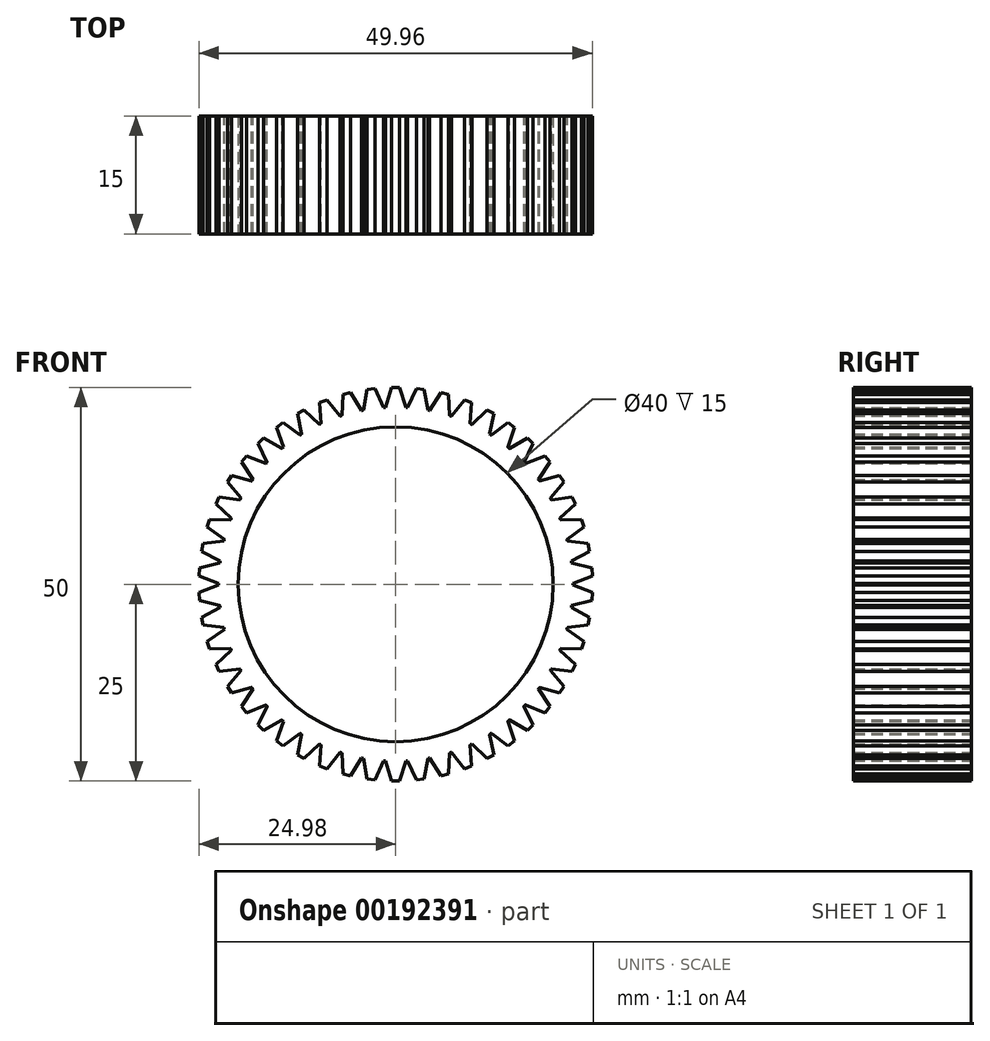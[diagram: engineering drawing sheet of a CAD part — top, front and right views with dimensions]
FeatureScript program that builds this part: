
annotation { "Feature Type Name" : "Feature", "Feature Type Description" : "" }
export const myFeature = defineFeature(function(context is Context, id is Id, definition is map)
    precondition{}
    {
        {
            var Q0;
            Q0=qCreatedBy(makeId("Front.planeOp"),FACE);
            var sketch = newSketch(context, id + "F0", { "sketchPlane" : qUnion([Q0])});
            skCircle(sketch, "E0", {"center": v(0, 0) * mm, "radius": 22.5 * mm});
            skLineSegment(sketch, "E1", {"start": v(-0.5, 25) * mm, "end": v(-1.3, 22.46) * mm});
            skLineSegment(sketch, "E2.MirrorCS", {"start": v(0.5, 25) * mm, "end": v(1.3, 22.46) * mm});
            skLineSegment(sketch, "E3", {"start": v(-0.5, 25) * mm, "end": v(0.5, 25) * mm});
            skLineSegment(sketch, "E4.1.0", {"start": v(-3.63, 24.74) * mm, "end": v(-2.64, 24.87) * mm});
            skLineSegment(sketch, "E4.1.1", {"start": v(-3.63, 24.74) * mm, "end": v(-4.1, 22.12) * mm});
            skLineSegment(sketch, "E4.1.2", {"start": v(-2.64, 24.87) * mm, "end": v(-1.53, 22.45) * mm});
            skLineSegment(sketch, "E4.2.0", {"start": v(-6.7, 24.1) * mm, "end": v(-5.73, 24.34) * mm});
            skLineSegment(sketch, "E4.2.1", {"start": v(-6.7, 24.1) * mm, "end": v(-6.84, 21.44) * mm});
            skLineSegment(sketch, "E4.2.2", {"start": v(-5.73, 24.34) * mm, "end": v(-4.33, 22.08) * mm});
            skLineSegment(sketch, "E4.3.0", {"start": v(-9.67, 23.06) * mm, "end": v(-8.74, 23.43) * mm});
            skLineSegment(sketch, "E4.3.1", {"start": v(-9.67, 23.06) * mm, "end": v(-9.47, 20.4) * mm});
            skLineSegment(sketch, "E4.3.2", {"start": v(-8.74, 23.43) * mm, "end": v(-7.07, 21.36) * mm});
            skLineSegment(sketch, "E4.4.0", {"start": v(-12.48, 21.67) * mm, "end": v(-11.6, 22.15) * mm});
            skLineSegment(sketch, "E4.4.1", {"start": v(-12.48, 21.67) * mm, "end": v(-11.95, 19.06) * mm});
            skLineSegment(sketch, "E4.4.2", {"start": v(-11.6, 22.15) * mm, "end": v(-9.69, 20.3) * mm});
            skLineSegment(sketch, "E4.5.0", {"start": v(-15.1, 19.93) * mm, "end": v(-14.3, 20.52) * mm});
            skLineSegment(sketch, "E4.5.1", {"start": v(-15.1, 19.93) * mm, "end": v(-14.25, 17.41) * mm});
            skLineSegment(sketch, "E4.5.2", {"start": v(-14.3, 20.52) * mm, "end": v(-12.16, 18.93) * mm});
            skLineSegment(sketch, "E4.6.0", {"start": v(-17.48, 17.88) * mm, "end": v(-16.75, 18.57) * mm});
            skLineSegment(sketch, "E4.6.1", {"start": v(-17.48, 17.88) * mm, "end": v(-16.32, 15.49) * mm});
            skLineSegment(sketch, "E4.6.2", {"start": v(-16.75, 18.57) * mm, "end": v(-14.43, 17.26) * mm});
            skLineSegment(sketch, "E4.7.0", {"start": v(-19.58, 15.55) * mm, "end": v(-18.94, 16.32) * mm});
            skLineSegment(sketch, "E4.7.1", {"start": v(-19.58, 15.55) * mm, "end": v(-18.13, 13.32) * mm});
            skLineSegment(sketch, "E4.7.2", {"start": v(-18.94, 16.32) * mm, "end": v(-16.48, 15.31) * mm});
            skLineSegment(sketch, "E4.8.0", {"start": v(-21.38, 12.97) * mm, "end": v(-20.84, 13.82) * mm});
            skLineSegment(sketch, "E4.8.1", {"start": v(-21.38, 12.97) * mm, "end": v(-19.66, 10.94) * mm});
            skLineSegment(sketch, "E4.8.2", {"start": v(-20.84, 13.82) * mm, "end": v(-18.27, 13.13) * mm});
            skLineSegment(sketch, "E4.9.0", {"start": v(-22.83, 10.2) * mm, "end": v(-22.4, 11.1) * mm});
            skLineSegment(sketch, "E4.9.1", {"start": v(-22.83, 10.2) * mm, "end": v(-20.88, 8.4) * mm});
            skLineSegment(sketch, "E4.9.2", {"start": v(-22.4, 11.1) * mm, "end": v(-19.77, 10.73) * mm});
            skLineSegment(sketch, "E4.10.0", {"start": v(-23.93, 7.25) * mm, "end": v(-23.62, 8.2) * mm});
            skLineSegment(sketch, "E4.10.1", {"start": v(-23.93, 7.25) * mm, "end": v(-21.76, 5.71) * mm});
            skLineSegment(sketch, "E4.10.2", {"start": v(-23.62, 8.2) * mm, "end": v(-20.96, 8.17) * mm});
            skLineSegment(sketch, "E4.11.0", {"start": v(-24.65, 4.2) * mm, "end": v(-24.46, 5.18) * mm});
            skLineSegment(sketch, "E4.11.1", {"start": v(-24.65, 4.2) * mm, "end": v(-22.3, 2.94) * mm});
            skLineSegment(sketch, "E4.11.2", {"start": v(-24.46, 5.18) * mm, "end": v(-21.82, 5.48) * mm});
            skLineSegment(sketch, "E4.12.0", {"start": v(-24.98, 1.07) * mm, "end": v(-24.92, 2.07) * mm});
            skLineSegment(sketch, "E4.12.1", {"start": v(-24.98, 1.07) * mm, "end": v(-22.5, 0.12) * mm});
            skLineSegment(sketch, "E4.12.2", {"start": v(-24.92, 2.07) * mm, "end": v(-22.34, 2.7) * mm});
            skLineSegment(sketch, "E4.13.0", {"start": v(-24.92, -2.07) * mm, "end": v(-24.98, -1.07) * mm});
            skLineSegment(sketch, "E4.13.1", {"start": v(-24.92, -2.07) * mm, "end": v(-22.34, -2.7) * mm});
            skLineSegment(sketch, "E4.13.2", {"start": v(-24.98, -1.07) * mm, "end": v(-22.5, -0.12) * mm});
            skLineSegment(sketch, "E4.14.0", {"start": v(-24.46, -5.18) * mm, "end": v(-24.65, -4.2) * mm});
            skLineSegment(sketch, "E4.14.1", {"start": v(-24.46, -5.18) * mm, "end": v(-21.82, -5.48) * mm});
            skLineSegment(sketch, "E4.14.2", {"start": v(-24.65, -4.2) * mm, "end": v(-22.3, -2.94) * mm});
            skLineSegment(sketch, "E4.15.0", {"start": v(-23.62, -8.2) * mm, "end": v(-23.93, -7.25) * mm});
            skLineSegment(sketch, "E4.15.1", {"start": v(-23.62, -8.2) * mm, "end": v(-20.96, -8.17) * mm});
            skLineSegment(sketch, "E4.15.2", {"start": v(-23.93, -7.25) * mm, "end": v(-21.76, -5.71) * mm});
            skLineSegment(sketch, "E4.16.0", {"start": v(-22.4, -11.1) * mm, "end": v(-22.83, -10.2) * mm});
            skLineSegment(sketch, "E4.16.1", {"start": v(-22.4, -11.1) * mm, "end": v(-19.77, -10.73) * mm});
            skLineSegment(sketch, "E4.16.2", {"start": v(-22.83, -10.2) * mm, "end": v(-20.88, -8.4) * mm});
            skLineSegment(sketch, "E4.17.0", {"start": v(-20.84, -13.82) * mm, "end": v(-21.38, -12.97) * mm});
            skLineSegment(sketch, "E4.17.1", {"start": v(-20.84, -13.82) * mm, "end": v(-18.27, -13.13) * mm});
            skLineSegment(sketch, "E4.17.2", {"start": v(-21.38, -12.97) * mm, "end": v(-19.66, -10.94) * mm});
            skLineSegment(sketch, "E4.18.0", {"start": v(-18.94, -16.32) * mm, "end": v(-19.58, -15.55) * mm});
            skLineSegment(sketch, "E4.18.1", {"start": v(-18.94, -16.32) * mm, "end": v(-16.48, -15.31) * mm});
            skLineSegment(sketch, "E4.18.2", {"start": v(-19.58, -15.55) * mm, "end": v(-18.13, -13.32) * mm});
            skLineSegment(sketch, "E4.19.0", {"start": v(-16.75, -18.57) * mm, "end": v(-17.48, -17.88) * mm});
            skLineSegment(sketch, "E4.19.1", {"start": v(-16.75, -18.57) * mm, "end": v(-14.43, -17.26) * mm});
            skLineSegment(sketch, "E4.19.2", {"start": v(-17.48, -17.88) * mm, "end": v(-16.32, -15.49) * mm});
            skLineSegment(sketch, "E4.20.0", {"start": v(-14.3, -20.52) * mm, "end": v(-15.1, -19.93) * mm});
            skLineSegment(sketch, "E4.20.1", {"start": v(-14.3, -20.52) * mm, "end": v(-12.16, -18.93) * mm});
            skLineSegment(sketch, "E4.20.2", {"start": v(-15.1, -19.93) * mm, "end": v(-14.25, -17.41) * mm});
            skLineSegment(sketch, "E4.21.0", {"start": v(-11.6, -22.15) * mm, "end": v(-12.48, -21.67) * mm});
            skLineSegment(sketch, "E4.21.1", {"start": v(-11.6, -22.15) * mm, "end": v(-9.69, -20.3) * mm});
            skLineSegment(sketch, "E4.21.2", {"start": v(-12.48, -21.67) * mm, "end": v(-11.95, -19.06) * mm});
            skLineSegment(sketch, "E4.22.0", {"start": v(-8.74, -23.43) * mm, "end": v(-9.67, -23.06) * mm});
            skLineSegment(sketch, "E4.22.1", {"start": v(-8.74, -23.43) * mm, "end": v(-7.07, -21.36) * mm});
            skLineSegment(sketch, "E4.22.2", {"start": v(-9.67, -23.06) * mm, "end": v(-9.47, -20.4) * mm});
            skLineSegment(sketch, "E4.23.0", {"start": v(-5.73, -24.34) * mm, "end": v(-6.7, -24.1) * mm});
            skLineSegment(sketch, "E4.23.1", {"start": v(-5.73, -24.34) * mm, "end": v(-4.33, -22.08) * mm});
            skLineSegment(sketch, "E4.23.2", {"start": v(-6.7, -24.1) * mm, "end": v(-6.84, -21.44) * mm});
            skLineSegment(sketch, "E4.24.0", {"start": v(-2.64, -24.87) * mm, "end": v(-3.63, -24.74) * mm});
            skLineSegment(sketch, "E4.24.1", {"start": v(-2.64, -24.87) * mm, "end": v(-1.53, -22.45) * mm});
            skLineSegment(sketch, "E4.24.2", {"start": v(-3.63, -24.74) * mm, "end": v(-4.1, -22.12) * mm});
            skLineSegment(sketch, "E4.25.0", {"start": v(0.5, -25) * mm, "end": v(-0.5, -25) * mm});
            skLineSegment(sketch, "E4.25.1", {"start": v(0.5, -25) * mm, "end": v(1.3, -22.46) * mm});
            skLineSegment(sketch, "E4.25.2", {"start": v(-0.5, -25) * mm, "end": v(-1.3, -22.46) * mm});
            skLineSegment(sketch, "E4.26.0", {"start": v(3.63, -24.74) * mm, "end": v(2.64, -24.87) * mm});
            skLineSegment(sketch, "E4.26.1", {"start": v(3.63, -24.74) * mm, "end": v(4.1, -22.12) * mm});
            skLineSegment(sketch, "E4.26.2", {"start": v(2.64, -24.87) * mm, "end": v(1.53, -22.45) * mm});
            skLineSegment(sketch, "E4.27.0", {"start": v(6.7, -24.1) * mm, "end": v(5.73, -24.34) * mm});
            skLineSegment(sketch, "E4.27.1", {"start": v(6.7, -24.1) * mm, "end": v(6.84, -21.44) * mm});
            skLineSegment(sketch, "E4.27.2", {"start": v(5.73, -24.34) * mm, "end": v(4.33, -22.08) * mm});
            skLineSegment(sketch, "E4.28.0", {"start": v(9.67, -23.06) * mm, "end": v(8.74, -23.43) * mm});
            skLineSegment(sketch, "E4.28.1", {"start": v(9.67, -23.06) * mm, "end": v(9.47, -20.4) * mm});
            skLineSegment(sketch, "E4.28.2", {"start": v(8.74, -23.43) * mm, "end": v(7.07, -21.36) * mm});
            skLineSegment(sketch, "E4.29.0", {"start": v(12.48, -21.67) * mm, "end": v(11.6, -22.15) * mm});
            skLineSegment(sketch, "E4.29.1", {"start": v(12.48, -21.67) * mm, "end": v(11.95, -19.06) * mm});
            skLineSegment(sketch, "E4.29.2", {"start": v(11.6, -22.15) * mm, "end": v(9.69, -20.3) * mm});
            skLineSegment(sketch, "E4.30.0", {"start": v(15.1, -19.93) * mm, "end": v(14.3, -20.52) * mm});
            skLineSegment(sketch, "E4.30.1", {"start": v(15.1, -19.93) * mm, "end": v(14.25, -17.41) * mm});
            skLineSegment(sketch, "E4.30.2", {"start": v(14.3, -20.52) * mm, "end": v(12.16, -18.93) * mm});
            skLineSegment(sketch, "E4.31.0", {"start": v(17.48, -17.88) * mm, "end": v(16.75, -18.57) * mm});
            skLineSegment(sketch, "E4.31.1", {"start": v(17.48, -17.88) * mm, "end": v(16.32, -15.49) * mm});
            skLineSegment(sketch, "E4.31.2", {"start": v(16.75, -18.57) * mm, "end": v(14.43, -17.26) * mm});
            skLineSegment(sketch, "E4.32.0", {"start": v(19.58, -15.55) * mm, "end": v(18.94, -16.32) * mm});
            skLineSegment(sketch, "E4.32.1", {"start": v(19.58, -15.55) * mm, "end": v(18.13, -13.32) * mm});
            skLineSegment(sketch, "E4.32.2", {"start": v(18.94, -16.32) * mm, "end": v(16.48, -15.31) * mm});
            skLineSegment(sketch, "E4.33.0", {"start": v(21.38, -12.97) * mm, "end": v(20.84, -13.82) * mm});
            skLineSegment(sketch, "E4.33.1", {"start": v(21.38, -12.97) * mm, "end": v(19.66, -10.94) * mm});
            skLineSegment(sketch, "E4.33.2", {"start": v(20.84, -13.82) * mm, "end": v(18.27, -13.13) * mm});
            skLineSegment(sketch, "E4.34.0", {"start": v(22.83, -10.2) * mm, "end": v(22.4, -11.1) * mm});
            skLineSegment(sketch, "E4.34.1", {"start": v(22.83, -10.2) * mm, "end": v(20.88, -8.4) * mm});
            skLineSegment(sketch, "E4.34.2", {"start": v(22.4, -11.1) * mm, "end": v(19.77, -10.73) * mm});
            skLineSegment(sketch, "E4.35.0", {"start": v(23.93, -7.25) * mm, "end": v(23.62, -8.2) * mm});
            skLineSegment(sketch, "E4.35.1", {"start": v(23.93, -7.25) * mm, "end": v(21.76, -5.71) * mm});
            skLineSegment(sketch, "E4.35.2", {"start": v(23.62, -8.2) * mm, "end": v(20.96, -8.17) * mm});
            skLineSegment(sketch, "E4.36.0", {"start": v(24.65, -4.2) * mm, "end": v(24.46, -5.18) * mm});
            skLineSegment(sketch, "E4.36.1", {"start": v(24.65, -4.2) * mm, "end": v(22.3, -2.94) * mm});
            skLineSegment(sketch, "E4.36.2", {"start": v(24.46, -5.18) * mm, "end": v(21.82, -5.48) * mm});
            skLineSegment(sketch, "E4.37.0", {"start": v(24.98, -1.07) * mm, "end": v(24.92, -2.07) * mm});
            skLineSegment(sketch, "E4.37.1", {"start": v(24.98, -1.07) * mm, "end": v(22.5, -0.12) * mm});
            skLineSegment(sketch, "E4.37.2", {"start": v(24.92, -2.07) * mm, "end": v(22.34, -2.7) * mm});
            skLineSegment(sketch, "E4.38.0", {"start": v(24.92, 2.07) * mm, "end": v(24.98, 1.07) * mm});
            skLineSegment(sketch, "E4.38.1", {"start": v(24.92, 2.07) * mm, "end": v(22.34, 2.7) * mm});
            skLineSegment(sketch, "E4.38.2", {"start": v(24.98, 1.07) * mm, "end": v(22.5, 0.12) * mm});
            skLineSegment(sketch, "E4.39.0", {"start": v(24.46, 5.18) * mm, "end": v(24.65, 4.2) * mm});
            skLineSegment(sketch, "E4.39.1", {"start": v(24.46, 5.18) * mm, "end": v(21.82, 5.48) * mm});
            skLineSegment(sketch, "E4.39.2", {"start": v(24.65, 4.2) * mm, "end": v(22.3, 2.94) * mm});
            skLineSegment(sketch, "E4.40.0", {"start": v(23.62, 8.2) * mm, "end": v(23.93, 7.25) * mm});
            skLineSegment(sketch, "E4.40.1", {"start": v(23.62, 8.2) * mm, "end": v(20.96, 8.17) * mm});
            skLineSegment(sketch, "E4.40.2", {"start": v(23.93, 7.25) * mm, "end": v(21.76, 5.71) * mm});
            skLineSegment(sketch, "E4.41.0", {"start": v(22.4, 11.1) * mm, "end": v(22.83, 10.2) * mm});
            skLineSegment(sketch, "E4.41.1", {"start": v(22.4, 11.1) * mm, "end": v(19.77, 10.73) * mm});
            skLineSegment(sketch, "E4.41.2", {"start": v(22.83, 10.2) * mm, "end": v(20.88, 8.4) * mm});
            skLineSegment(sketch, "E4.42.0", {"start": v(20.84, 13.82) * mm, "end": v(21.38, 12.97) * mm});
            skLineSegment(sketch, "E4.42.1", {"start": v(20.84, 13.82) * mm, "end": v(18.27, 13.13) * mm});
            skLineSegment(sketch, "E4.42.2", {"start": v(21.38, 12.97) * mm, "end": v(19.66, 10.94) * mm});
            skLineSegment(sketch, "E4.43.0", {"start": v(18.94, 16.32) * mm, "end": v(19.58, 15.55) * mm});
            skLineSegment(sketch, "E4.43.1", {"start": v(18.94, 16.32) * mm, "end": v(16.48, 15.31) * mm});
            skLineSegment(sketch, "E4.43.2", {"start": v(19.58, 15.55) * mm, "end": v(18.13, 13.32) * mm});
            skLineSegment(sketch, "E4.44.0", {"start": v(16.75, 18.57) * mm, "end": v(17.48, 17.88) * mm});
            skLineSegment(sketch, "E4.44.1", {"start": v(16.75, 18.57) * mm, "end": v(14.43, 17.26) * mm});
            skLineSegment(sketch, "E4.44.2", {"start": v(17.48, 17.88) * mm, "end": v(16.32, 15.49) * mm});
            skLineSegment(sketch, "E4.45.0", {"start": v(14.3, 20.52) * mm, "end": v(15.1, 19.93) * mm});
            skLineSegment(sketch, "E4.45.1", {"start": v(14.3, 20.52) * mm, "end": v(12.16, 18.93) * mm});
            skLineSegment(sketch, "E4.45.2", {"start": v(15.1, 19.93) * mm, "end": v(14.25, 17.41) * mm});
            skLineSegment(sketch, "E4.46.0", {"start": v(11.6, 22.15) * mm, "end": v(12.48, 21.67) * mm});
            skLineSegment(sketch, "E4.46.1", {"start": v(11.6, 22.15) * mm, "end": v(9.69, 20.3) * mm});
            skLineSegment(sketch, "E4.46.2", {"start": v(12.48, 21.67) * mm, "end": v(11.95, 19.06) * mm});
            skLineSegment(sketch, "E4.47.0", {"start": v(8.74, 23.43) * mm, "end": v(9.67, 23.06) * mm});
            skLineSegment(sketch, "E4.47.1", {"start": v(8.74, 23.43) * mm, "end": v(7.07, 21.36) * mm});
            skLineSegment(sketch, "E4.47.2", {"start": v(9.67, 23.06) * mm, "end": v(9.47, 20.4) * mm});
            skLineSegment(sketch, "E4.48.0", {"start": v(5.73, 24.34) * mm, "end": v(6.7, 24.1) * mm});
            skLineSegment(sketch, "E4.48.1", {"start": v(5.73, 24.34) * mm, "end": v(4.33, 22.08) * mm});
            skLineSegment(sketch, "E4.48.2", {"start": v(6.7, 24.1) * mm, "end": v(6.84, 21.44) * mm});
            skLineSegment(sketch, "E4.49.0", {"start": v(2.64, 24.87) * mm, "end": v(3.63, 24.74) * mm});
            skLineSegment(sketch, "E4.49.1", {"start": v(2.64, 24.87) * mm, "end": v(1.53, 22.45) * mm});
            skLineSegment(sketch, "E4.49.2", {"start": v(3.63, 24.74) * mm, "end": v(4.1, 22.12) * mm});
            skSolve(sketch);
        }
        {
            var Q0;
            Q0 = qSketchRegion(id + "F0", true);
            extrude(context, id + "F1", {"entities" : qUnion([Q0]), "depth" : 15 * mm});
        }
        {
            var Q0;
            Q0=makeQuery(id+"F1.opExtrude","CAP_FACE",FACE,{"disambiguationData":[OSD([sQuery(id+"F0.wireOp",EDGE,"E0"),sQuery(id+"F0.wireOp",EDGE,"E1"),sQuery(id+"F0.wireOp",EDGE,"E2.MirrorCS"),sQuery(id+"F0.wireOp",EDGE,"E3"),sQuery(id+"F0.wireOp",EDGE,"E4.1.0"),sQuery(id+"F0.wireOp",EDGE,"E4.1.1"),sQuery(id+"F0.wireOp",EDGE,"E4.1.2"),sQuery(id+"F0.wireOp",EDGE,"E4.2.0"),sQuery(id+"F0.wireOp",EDGE,"E4.2.1"),sQuery(id+"F0.wireOp",EDGE,"E4.2.2"),sQuery(id+"F0.wireOp",EDGE,"E4.3.0"),sQuery(id+"F0.wireOp",EDGE,"E4.3.1"),sQuery(id+"F0.wireOp",EDGE,"E4.3.2"),sQuery(id+"F0.wireOp",EDGE,"E4.4.0"),sQuery(id+"F0.wireOp",EDGE,"E4.4.1"),sQuery(id+"F0.wireOp",EDGE,"E4.4.2"),sQuery(id+"F0.wireOp",EDGE,"E4.5.0"),sQuery(id+"F0.wireOp",EDGE,"E4.5.1"),sQuery(id+"F0.wireOp",EDGE,"E4.5.2"),sQuery(id+"F0.wireOp",EDGE,"E4.6.0"),sQuery(id+"F0.wireOp",EDGE,"E4.6.1"),sQuery(id+"F0.wireOp",EDGE,"E4.6.2"),sQuery(id+"F0.wireOp",EDGE,"E4.7.0"),sQuery(id+"F0.wireOp",EDGE,"E4.7.1"),sQuery(id+"F0.wireOp",EDGE,"E4.7.2"),sQuery(id+"F0.wireOp",EDGE,"E4.8.0"),sQuery(id+"F0.wireOp",EDGE,"E4.8.1"),sQuery(id+"F0.wireOp",EDGE,"E4.8.2"),sQuery(id+"F0.wireOp",EDGE,"E4.9.0"),sQuery(id+"F0.wireOp",EDGE,"E4.9.1"),sQuery(id+"F0.wireOp",EDGE,"E4.9.2"),sQuery(id+"F0.wireOp",EDGE,"E4.10.0"),sQuery(id+"F0.wireOp",EDGE,"E4.10.1"),sQuery(id+"F0.wireOp",EDGE,"E4.10.2"),sQuery(id+"F0.wireOp",EDGE,"E4.11.0"),sQuery(id+"F0.wireOp",EDGE,"E4.11.1"),sQuery(id+"F0.wireOp",EDGE,"E4.11.2"),sQuery(id+"F0.wireOp",EDGE,"E4.12.0"),sQuery(id+"F0.wireOp",EDGE,"E4.12.1"),sQuery(id+"F0.wireOp",EDGE,"E4.12.2"),sQuery(id+"F0.wireOp",EDGE,"E4.13.0"),sQuery(id+"F0.wireOp",EDGE,"E4.13.1"),sQuery(id+"F0.wireOp",EDGE,"E4.13.2"),sQuery(id+"F0.wireOp",EDGE,"E4.14.0"),sQuery(id+"F0.wireOp",EDGE,"E4.14.1"),sQuery(id+"F0.wireOp",EDGE,"E4.14.2"),sQuery(id+"F0.wireOp",EDGE,"E4.15.0"),sQuery(id+"F0.wireOp",EDGE,"E4.15.1"),sQuery(id+"F0.wireOp",EDGE,"E4.15.2"),sQuery(id+"F0.wireOp",EDGE,"E4.16.0"),sQuery(id+"F0.wireOp",EDGE,"E4.16.1"),sQuery(id+"F0.wireOp",EDGE,"E4.16.2"),sQuery(id+"F0.wireOp",EDGE,"E4.17.0"),sQuery(id+"F0.wireOp",EDGE,"E4.17.1"),sQuery(id+"F0.wireOp",EDGE,"E4.17.2"),sQuery(id+"F0.wireOp",EDGE,"E4.18.0"),sQuery(id+"F0.wireOp",EDGE,"E4.18.1"),sQuery(id+"F0.wireOp",EDGE,"E4.18.2"),sQuery(id+"F0.wireOp",EDGE,"E4.19.0"),sQuery(id+"F0.wireOp",EDGE,"E4.19.1"),sQuery(id+"F0.wireOp",EDGE,"E4.19.2"),sQuery(id+"F0.wireOp",EDGE,"E4.20.0"),sQuery(id+"F0.wireOp",EDGE,"E4.20.1"),sQuery(id+"F0.wireOp",EDGE,"E4.20.2"),sQuery(id+"F0.wireOp",EDGE,"E4.21.0"),sQuery(id+"F0.wireOp",EDGE,"E4.21.1"),sQuery(id+"F0.wireOp",EDGE,"E4.21.2"),sQuery(id+"F0.wireOp",EDGE,"E4.22.0"),sQuery(id+"F0.wireOp",EDGE,"E4.22.1"),sQuery(id+"F0.wireOp",EDGE,"E4.22.2"),sQuery(id+"F0.wireOp",EDGE,"E4.23.0"),sQuery(id+"F0.wireOp",EDGE,"E4.23.1"),sQuery(id+"F0.wireOp",EDGE,"E4.23.2"),sQuery(id+"F0.wireOp",EDGE,"E4.24.0"),sQuery(id+"F0.wireOp",EDGE,"E4.24.1"),sQuery(id+"F0.wireOp",EDGE,"E4.24.2"),sQuery(id+"F0.wireOp",EDGE,"E4.25.0"),sQuery(id+"F0.wireOp",EDGE,"E4.25.1"),sQuery(id+"F0.wireOp",EDGE,"E4.25.2"),sQuery(id+"F0.wireOp",EDGE,"E4.26.0"),sQuery(id+"F0.wireOp",EDGE,"E4.26.1"),sQuery(id+"F0.wireOp",EDGE,"E4.26.2"),sQuery(id+"F0.wireOp",EDGE,"E4.27.0"),sQuery(id+"F0.wireOp",EDGE,"E4.27.1"),sQuery(id+"F0.wireOp",EDGE,"E4.27.2"),sQuery(id+"F0.wireOp",EDGE,"E4.28.0"),sQuery(id+"F0.wireOp",EDGE,"E4.28.1"),sQuery(id+"F0.wireOp",EDGE,"E4.28.2"),sQuery(id+"F0.wireOp",EDGE,"E4.29.0"),sQuery(id+"F0.wireOp",EDGE,"E4.29.1"),sQuery(id+"F0.wireOp",EDGE,"E4.29.2"),sQuery(id+"F0.wireOp",EDGE,"E4.30.0"),sQuery(id+"F0.wireOp",EDGE,"E4.30.1"),sQuery(id+"F0.wireOp",EDGE,"E4.30.2"),sQuery(id+"F0.wireOp",EDGE,"E4.31.0"),sQuery(id+"F0.wireOp",EDGE,"E4.31.1"),sQuery(id+"F0.wireOp",EDGE,"E4.31.2"),sQuery(id+"F0.wireOp",EDGE,"E4.32.0"),sQuery(id+"F0.wireOp",EDGE,"E4.32.1"),sQuery(id+"F0.wireOp",EDGE,"E4.32.2"),sQuery(id+"F0.wireOp",EDGE,"E4.33.0"),sQuery(id+"F0.wireOp",EDGE,"E4.33.1"),sQuery(id+"F0.wireOp",EDGE,"E4.33.2"),sQuery(id+"F0.wireOp",EDGE,"E4.34.0"),sQuery(id+"F0.wireOp",EDGE,"E4.34.1"),sQuery(id+"F0.wireOp",EDGE,"E4.34.2"),sQuery(id+"F0.wireOp",EDGE,"E4.35.0"),sQuery(id+"F0.wireOp",EDGE,"E4.35.1"),sQuery(id+"F0.wireOp",EDGE,"E4.35.2"),sQuery(id+"F0.wireOp",EDGE,"E4.36.0"),sQuery(id+"F0.wireOp",EDGE,"E4.36.1"),sQuery(id+"F0.wireOp",EDGE,"E4.36.2"),sQuery(id+"F0.wireOp",EDGE,"E4.37.0"),sQuery(id+"F0.wireOp",EDGE,"E4.37.1"),sQuery(id+"F0.wireOp",EDGE,"E4.37.2"),sQuery(id+"F0.wireOp",EDGE,"E4.38.0"),sQuery(id+"F0.wireOp",EDGE,"E4.38.1"),sQuery(id+"F0.wireOp",EDGE,"E4.38.2"),sQuery(id+"F0.wireOp",EDGE,"E4.39.0"),sQuery(id+"F0.wireOp",EDGE,"E4.39.1"),sQuery(id+"F0.wireOp",EDGE,"E4.39.2"),sQuery(id+"F0.wireOp",EDGE,"E4.40.0"),sQuery(id+"F0.wireOp",EDGE,"E4.40.1"),sQuery(id+"F0.wireOp",EDGE,"E4.40.2"),sQuery(id+"F0.wireOp",EDGE,"E4.41.0"),sQuery(id+"F0.wireOp",EDGE,"E4.41.1"),sQuery(id+"F0.wireOp",EDGE,"E4.41.2"),sQuery(id+"F0.wireOp",EDGE,"E4.42.0"),sQuery(id+"F0.wireOp",EDGE,"E4.42.1"),sQuery(id+"F0.wireOp",EDGE,"E4.42.2"),sQuery(id+"F0.wireOp",EDGE,"E4.43.0"),sQuery(id+"F0.wireOp",EDGE,"E4.43.1"),sQuery(id+"F0.wireOp",EDGE,"E4.43.2"),sQuery(id+"F0.wireOp",EDGE,"E4.44.0"),sQuery(id+"F0.wireOp",EDGE,"E4.44.1"),sQuery(id+"F0.wireOp",EDGE,"E4.44.2"),sQuery(id+"F0.wireOp",EDGE,"E4.45.0"),sQuery(id+"F0.wireOp",EDGE,"E4.45.1"),sQuery(id+"F0.wireOp",EDGE,"E4.45.2"),sQuery(id+"F0.wireOp",EDGE,"E4.46.0"),sQuery(id+"F0.wireOp",EDGE,"E4.46.1"),sQuery(id+"F0.wireOp",EDGE,"E4.46.2"),sQuery(id+"F0.wireOp",EDGE,"E4.47.0"),sQuery(id+"F0.wireOp",EDGE,"E4.47.1"),sQuery(id+"F0.wireOp",EDGE,"E4.47.2"),sQuery(id+"F0.wireOp",EDGE,"E4.48.0"),sQuery(id+"F0.wireOp",EDGE,"E4.48.1"),sQuery(id+"F0.wireOp",EDGE,"E4.48.2"),sQuery(id+"F0.wireOp",EDGE,"E4.49.0"),sQuery(id+"F0.wireOp",EDGE,"E4.49.1"),sQuery(id+"F0.wireOp",EDGE,"E4.49.2")])],"isStart":false});
            var sketch = newSketch(context, id + "F2", { "sketchPlane" : qUnion([Q0])});
            skCircle(sketch, "E5", {"center": v(0, 0) * mm, "radius": 20 * mm});
            skSolve(sketch);
        }
        {
            var Q0;
            Q0 = qSketchRegion(id + "F2", true);
            extrude(context, id + "F3", {"entities" : qUnion([Q0]), "operationType" : NewBodyOperationType.REMOVE, "endBound" : BoundingType.UP_TO_NEXT, "oppositeDirection" : true, "depth" : 25 * mm});
        }
    });
